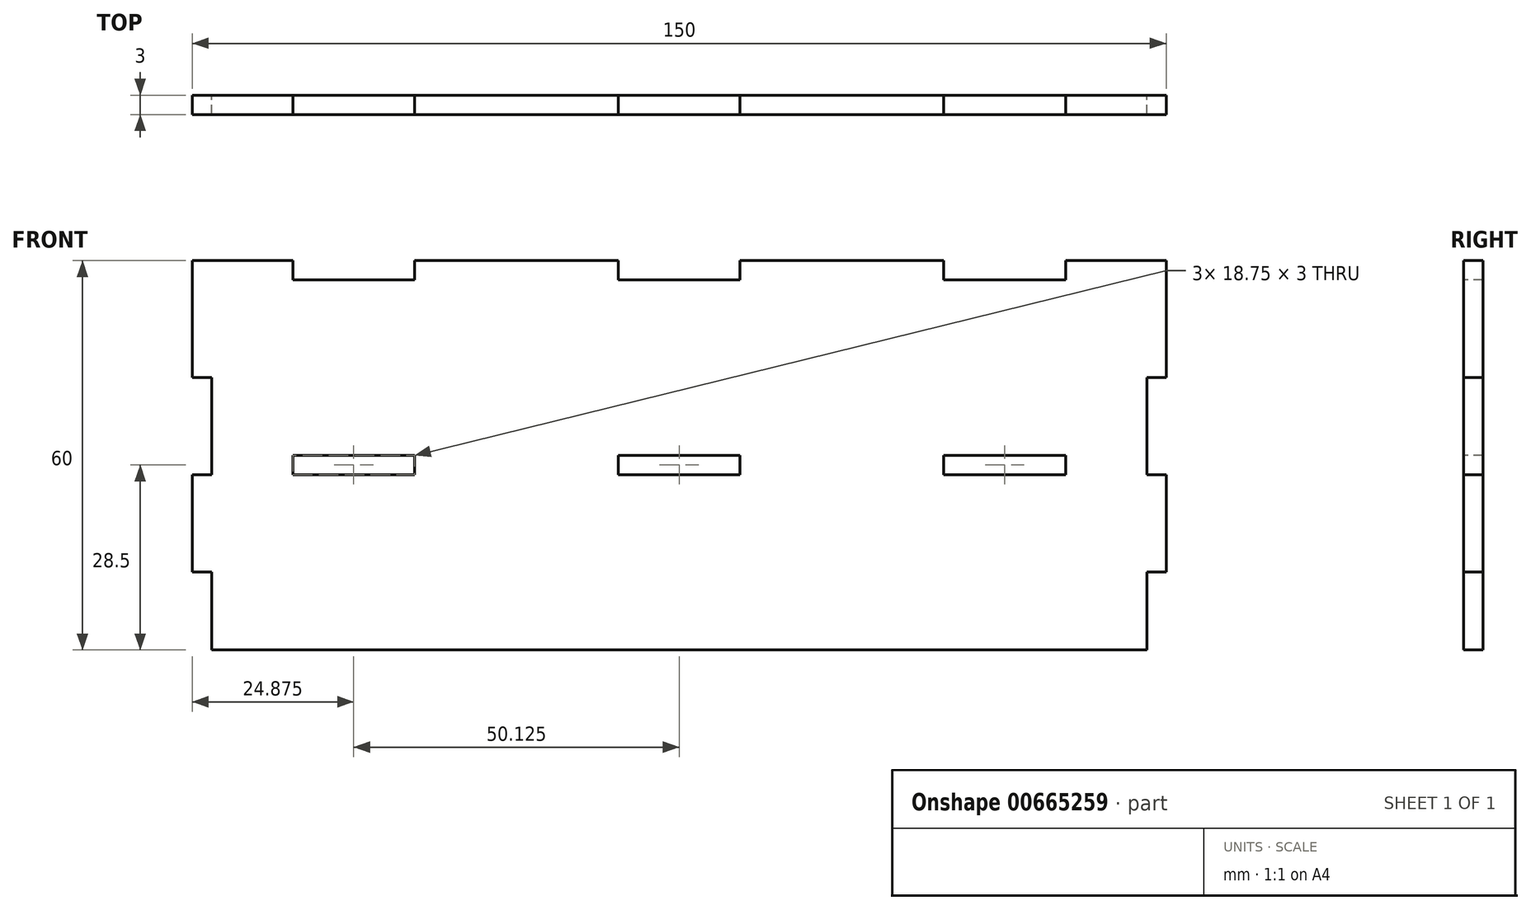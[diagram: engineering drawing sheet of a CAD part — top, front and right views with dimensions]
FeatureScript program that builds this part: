
annotation { "Feature Type Name" : "Feature", "Feature Type Description" : "" }
export const myFeature = defineFeature(function(context is Context, id is Id, definition is map)
    precondition{}
    {
        {
            var Q0;
            Q0=qCreatedBy(makeId("Front.planeOp"),FACE);
            var sketch = newSketch(context, id + "F0", { "sketchPlane" : qUnion([Q0])});
            skLineSegment(sketch, "E0.bottom", {"start": v(-75, 30) * mm, "end": v(75, 30) * mm});
            skLineSegment(sketch, "E0.top", {"start": v(-75, -30) * mm, "end": v(75, -30) * mm});
            skLineSegment(sketch, "E0.left", {"start": v(-75, 30) * mm, "end": v(-75, -30) * mm});
            skLineSegment(sketch, "E0.right", {"start": v(75, 30) * mm, "end": v(75, -30) * mm});
            skPoint(sketch, "E0.middle", {"position": v(0, 0) * mm});
            skSolve(sketch);
        }
        {
            var Q0;
            Q0 = qSketchRegion(id + "F0", true);
            extrude(context, id + "F1", {"entities" : qUnion([Q0]), "depth" : 3 * mm, "offsetDistance" : 25 * mm});
        }
        {
            var Q0;
            Q0=makeQuery(id+"F1.opExtrude","CAP_FACE",FACE,{"disambiguationData":[OSD([sQuery(id+"F0.wireOp",EDGE,"E0.bottom"),sQuery(id+"F0.wireOp",EDGE,"E0.top"),sQuery(id+"F0.wireOp",EDGE,"E0.left"),sQuery(id+"F0.wireOp",EDGE,"E0.right")])],"isStart":false});
            var sketch = newSketch(context, id + "F2", { "sketchPlane" : qUnion([Q0])});
            skLineSegment(sketch, "E1.bottom", {"start": v(-59.5, 30) * mm, "end": v(-40.75, 30) * mm});
            skLineSegment(sketch, "E1.top", {"start": v(-59.5, 27) * mm, "end": v(-40.75, 27) * mm});
            skLineSegment(sketch, "E1.left", {"start": v(-59.5, 30) * mm, "end": v(-59.5, 27) * mm});
            skLineSegment(sketch, "E1.right", {"start": v(-40.75, 30) * mm, "end": v(-40.75, 27) * mm});
            skLineSegment(sketch, "E2.0.1.0", {"start": v(-59.5, -3) * mm, "end": v(-40.75, -3) * mm});
            skLineSegment(sketch, "E2.0.1.1", {"start": v(-59.5, 0) * mm, "end": v(-40.75, 0) * mm});
            skLineSegment(sketch, "E2.0.1.2", {"start": v(-59.5, 0) * mm, "end": v(-59.5, -3) * mm});
            skLineSegment(sketch, "E2.0.1.3", {"start": v(-40.75, 0) * mm, "end": v(-40.75, -3) * mm});
            skLineSegment(sketch, "E2.1.0.0", {"start": v(-9.37, 27) * mm, "end": v(9.38, 27) * mm});
            skLineSegment(sketch, "E2.1.0.1", {"start": v(-9.37, 30) * mm, "end": v(9.38, 30) * mm});
            skLineSegment(sketch, "E2.1.0.2", {"start": v(-9.37, 30) * mm, "end": v(-9.37, 27) * mm});
            skLineSegment(sketch, "E2.1.0.3", {"start": v(9.38, 30) * mm, "end": v(9.38, 27) * mm});
            skLineSegment(sketch, "E2.1.1.0", {"start": v(-9.37, -3) * mm, "end": v(9.38, -3) * mm});
            skLineSegment(sketch, "E2.1.1.1", {"start": v(-9.37, 0) * mm, "end": v(9.38, 0) * mm});
            skLineSegment(sketch, "E2.1.1.2", {"start": v(-9.37, 0) * mm, "end": v(-9.37, -3) * mm});
            skLineSegment(sketch, "E2.1.1.3", {"start": v(9.38, 0) * mm, "end": v(9.38, -3) * mm});
            skLineSegment(sketch, "E2.2.0.0", {"start": v(40.75, 27) * mm, "end": v(59.5, 27) * mm});
            skLineSegment(sketch, "E2.2.0.1", {"start": v(40.75, 30) * mm, "end": v(59.5, 30) * mm});
            skLineSegment(sketch, "E2.2.0.2", {"start": v(40.75, 30) * mm, "end": v(40.75, 27) * mm});
            skLineSegment(sketch, "E2.2.0.3", {"start": v(59.5, 30) * mm, "end": v(59.5, 27) * mm});
            skLineSegment(sketch, "E2.2.1.0", {"start": v(40.75, -3) * mm, "end": v(59.5, -3) * mm});
            skLineSegment(sketch, "E2.2.1.1", {"start": v(40.75, 0) * mm, "end": v(59.5, 0) * mm});
            skLineSegment(sketch, "E2.2.1.2", {"start": v(40.75, 0) * mm, "end": v(40.75, -3) * mm});
            skLineSegment(sketch, "E2.2.1.3", {"start": v(59.5, 0) * mm, "end": v(59.5, -3) * mm});
            skLineSegment(sketch, "E2.direction1", {"start": v(-59.5, 27) * mm, "end": v(-9.37, 27) * mm, "construction": true});
            skLineSegment(sketch, "E2.direction2", {"start": v(-59.5, 27) * mm, "end": v(-59.5, -3) * mm, "construction": true});
            skSolve(sketch);
        }
        {
            var Q0;
            Q0 = qSketchRegion(id + "F2", true);
            extrude(context, id + "F3", {"entities" : qUnion([Q0]), "operationType" : NewBodyOperationType.REMOVE, "endBound" : BoundingType.UP_TO_NEXT, "oppositeDirection" : true, "depth" : 25 * mm, "offsetDistance" : 25 * mm});
        }
        {
            var Q0;
            Q0=makeQuery(id+"F1.opExtrude","CAP_FACE",FACE,{"disambiguationData":[OSD([sQuery(id+"F0.wireOp",EDGE,"E0.bottom"),sQuery(id+"F0.wireOp",EDGE,"E0.top"),sQuery(id+"F0.wireOp",EDGE,"E0.left"),sQuery(id+"F0.wireOp",EDGE,"E0.right")])],"isStart":false});
            var sketch = newSketch(context, id + "F4", { "sketchPlane" : qUnion([Q0])});
            skLineSegment(sketch, "E3.bottom", {"start": v(-75, 12) * mm, "end": v(-72, 12) * mm});
            skLineSegment(sketch, "E3.top", {"start": v(-75, -3) * mm, "end": v(-72, -3) * mm});
            skLineSegment(sketch, "E3.left", {"start": v(-75, 12) * mm, "end": v(-75, -3) * mm});
            skLineSegment(sketch, "E3.right", {"start": v(-72, 12) * mm, "end": v(-72, -3) * mm});
            skLineSegment(sketch, "E4.0.1.0", {"start": v(-72, -18) * mm, "end": v(-72, -33) * mm});
            skLineSegment(sketch, "E4.0.1.1", {"start": v(-75, -33) * mm, "end": v(-72, -33) * mm});
            skLineSegment(sketch, "E4.0.1.2", {"start": v(-75, -18) * mm, "end": v(-72, -18) * mm});
            skLineSegment(sketch, "E4.0.1.3", {"start": v(-75, -18) * mm, "end": v(-75, -33) * mm});
            skLineSegment(sketch, "E4.1.0.0", {"start": v(75, 12) * mm, "end": v(75, -3) * mm});
            skLineSegment(sketch, "E4.1.0.1", {"start": v(72, -3) * mm, "end": v(75, -3) * mm});
            skLineSegment(sketch, "E4.1.0.2", {"start": v(72, 12) * mm, "end": v(75, 12) * mm});
            skLineSegment(sketch, "E4.1.0.3", {"start": v(72, 12) * mm, "end": v(72, -3) * mm});
            skLineSegment(sketch, "E4.1.1.0", {"start": v(75, -18) * mm, "end": v(75, -33) * mm});
            skLineSegment(sketch, "E4.1.1.1", {"start": v(72, -33) * mm, "end": v(75, -33) * mm});
            skLineSegment(sketch, "E4.1.1.2", {"start": v(72, -18) * mm, "end": v(75, -18) * mm});
            skLineSegment(sketch, "E4.1.1.3", {"start": v(72, -18) * mm, "end": v(72, -33) * mm});
            skLineSegment(sketch, "E4.direction1", {"start": v(-75, -3) * mm, "end": v(72, -3) * mm, "construction": true});
            skLineSegment(sketch, "E4.direction2", {"start": v(-75, -3) * mm, "end": v(-75, -33) * mm, "construction": true});
            skSolve(sketch);
        }
        {
            var Q0;
            Q0 = qSketchRegion(id + "F4", true);
            extrude(context, id + "F5", {"entities" : qUnion([Q0]), "operationType" : NewBodyOperationType.REMOVE, "endBound" : BoundingType.UP_TO_NEXT, "oppositeDirection" : true, "depth" : 25 * mm, "offsetDistance" : 25 * mm});
        }
    });
